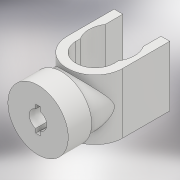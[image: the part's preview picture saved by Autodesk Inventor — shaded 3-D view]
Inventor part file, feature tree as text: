
AUTODESK INVENTOR PART (.ipt)
format: ipt  version: 2018.2 (Build 222227000, 227)  size: 200,192 bytes
history: native  units: mm
features: extrude x6, sketch x5, fillet x2
ambient origin geometry x8: Origin, YZ Plane, XZ Plane, XY Plane, X Axis, Y Axis, Z Axis, Center Point
bodies: Solid1 (feature_tree)
feature tree (13):
  extrude  "Extrusion1"  Depth=9.0mm
  extrude  "Extrusion5"  Depth=3.5mm
  extrude  "Extrusion6"  Depth=7.3mm
  extrude  "Extrusion2"  Depth=8.0mm TaperAngle=0.0deg
  sketch  "Sketch3"  dims[d7=18.0mm d8=0.0mm d9=7.3mm]
  extrude  "Extrusion3"  Depth=1.0mm
  extrude  "Extrusion4"  Depth=1.0mm
  fillet  "Fillet1"  Radius=0.26mm
  fillet  "Fillet2"  Radius=0.7mm
  sketch  "Sketch1"  dims[d1=2.1mm d3=9.0mm]
  sketch  "Sketch2"  dims[d4=3.5mm d5=0.0mm d6=2.0mm]
  sketch  "Sketch4"  dims[d10=2.0mm d11=8.0mm d12=0.0mm]
  sketch  "Sketch8"  dims[d13=12.0mm d14=0.0mm d15=1.0mm d16=1.0mm d18=0.26mm d19=0.7mm d20=3.75mm d21=2.85mm d23=1.3mm d24=5.0mm d25=7.0mm d26=6.8mm d27=2.5mm d28=9.0mm d29=0.0mm d33=8.0mm d34=9.0mm d35=0.0mm]
